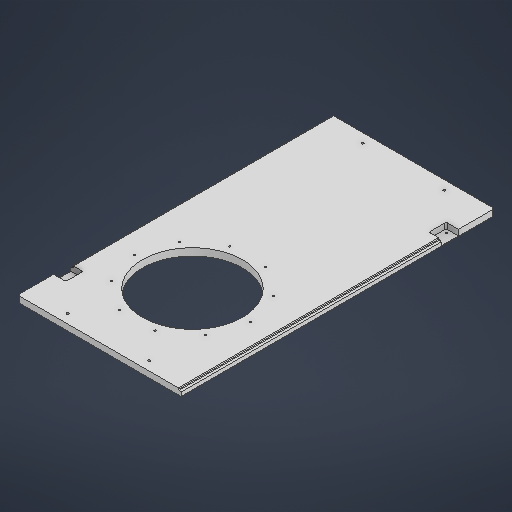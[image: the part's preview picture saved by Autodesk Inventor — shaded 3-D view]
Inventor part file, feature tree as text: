
AUTODESK INVENTOR PART (.ipt)
format: ipt  version: 2025 (Build 290162000, 162)  size: 337,408 bytes
history: native  units: in
note: dims shown in document units (in); Inventor stores cm internally (conversion verified against a paired STEP export)
features: sketch x9, chamfer x5, extrude x4, hole x3, plane x2, fillet x1
ambient origin geometry x8: Origin, YZ Plane, XZ Plane, XY Plane, X Axis, Y Axis, Z Axis, Center Point
bodies: Solid1 (feature_tree)
feature tree (24):
  extrude  "Extrusion1"  Depth=27.1654in
  sketch  "Sketch2"  dims[d2=0.625in d3=0.0in d4=8.0709in]
  extrude  "Extrusion2"  Depth=0.625in
  plane  "Work Plane1"
  hole  "Hole3"  [1 undecoded]
  sketch  "Sketch7"  dims[d56=25.5906in]
  plane  "Work Plane2"
  hole  "Hole4"  [1 undecoded]
  sketch  "Sketch9"  dims[d65=10.6299in d68=10.0394in]
  fillet  "Fillet2"  Radius=7.0625in
  extrude  "Extrusion7"  Depth=0.1969in
  extrude  "Extrusion8"  Depth=10.0394in
  chamfer  "Chamfer3"  Distance=3.937in Angle=360.0deg
  chamfer  "Chamfer4"  Distance=1.063in
  hole  "Hole5"  [1 undecoded]
  chamfer  "Chamfer5"  Distance=1.4961in
  chamfer  "Chamfer6"  Distance=1.4961in
  chamfer  "Chamfer7"  Distance=3.1102in
  sketch  "Sketch1"  dims[d0=14.1732in d1=27.1654in]
  sketch  "Sketch6"  dims[d8=10.6299in d50=5.9055in d55=7.0625in]
  sketch  "Sketch8"  dims[d57=0.1936in d58=0.1969in d59=0.1575in d60=0.0787in d61=90.0deg d62=0.1969in d63=0.8108in d64=10.3543in]
  sketch  "Sketch Circular Pattern4"  dims[d5=8.6614in d6=0.0in d7=0.0in]
  sketch  "Sketch10"  dims[d69=0.1575in d70=3.937in d72=360.0deg]
  sketch  "Sketch11"  dims[d74=0.1628in d75=0.3937in d76=0.1575in d77=0.0787in d78=90.0deg d79=0.3937in d80=0.8108in d82=1.063in d83=1.063in d84=1.4961in d85=1.4961in d86=3.1102in d87=3.1102in d88=0.1969in d95=0.1181in d96=0.1181in d97=0.4951in d98=0.0in d99=0.2362in d100=0.2362in d101=0.122in d102=0.0in d103=0.0787in d104=0.1378in d105=45.0deg d106=0.1378in d107=0.0787in d108=45.0deg d109=0.748in d110=0.315in d111=0.8661in d112=0.748in d113=0.1299in d114=0.1299in d115=0.1299in d116=0.1299in d118=0.315in d119=0.8661in d120=0.748in d121=0.748in d122=0.1276in d123=0.315in d124=0.1575in d125=0.0787in d126=90.0deg d127=0.315in d128=0.8108in d129=0.0138in d130=0.0787in d131=45.0deg d146=0.0984in d147=0.0787in d148=45.0deg d149=0.0984in d150=0.0787in d151=45.0deg d26=0.0394in d27=0.0394in d28=0.0394in d29=0.0059in d30=0.0098in d31=0.0148in d32=0.5635in d33=0.0295in d34=0.8108in d35=0.0025in d36=0.0295in d37=0.0148in d66=0.0197in d67=0.0344in]
note: 3 required parameter values undecoded (feature->parameter linkage not recoverable at this tier; creation-order binding heuristic only, values carry confidence <= 0.55)
